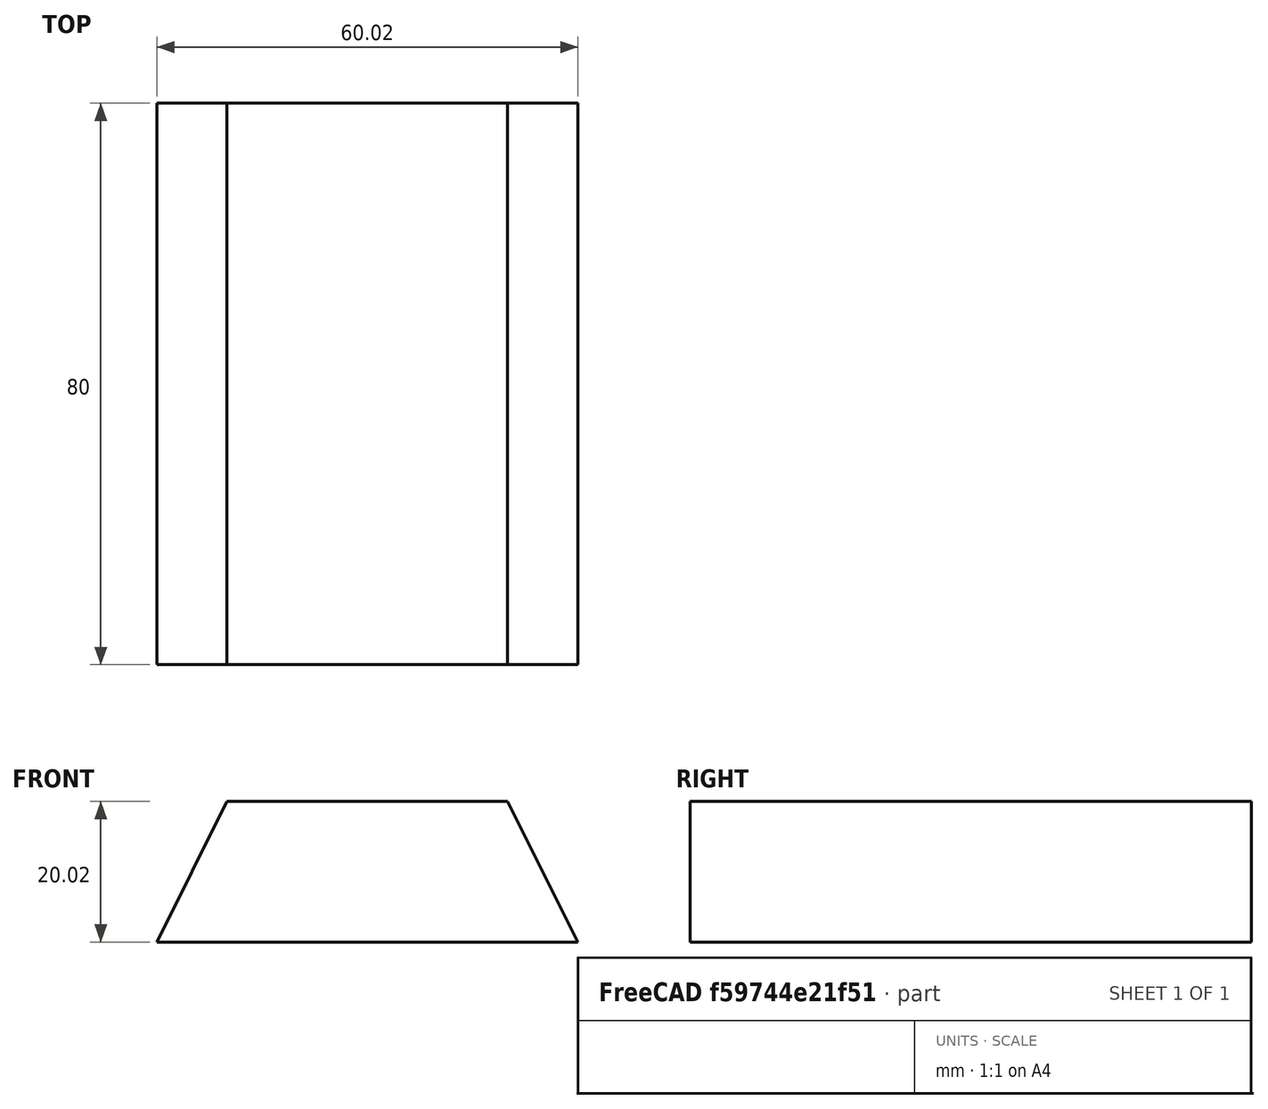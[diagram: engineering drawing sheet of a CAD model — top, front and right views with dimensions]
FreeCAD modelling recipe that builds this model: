
FCSTD DOCUMENT  (FreeCAD 0.21R33694 (Git))
Label: OJT1_T016R01_lingot_or
License: All rights reserved
LicenseURL: http://en.wikipedia.org/wiki/All_rights_reserved
objects: Sketcher::SketchObject×1, PartDesign::Pad×1, PartDesign::Body×1
note: 4 computed .brp shape members not serialized (recipe doc carries the construction recipe); baked Part::Feature solids carry a one-line shape summary decoded from their .brp

FEATURE [Sketcher::SketchObject] Sketch
  FullyConstrained = false
  MapMode = 5
  Support = -> [XY_Plane]
  sketch-geometry (4):
    g0: LineSegment StartX=-19.8368 StartY=20.0225 StartZ=0 EndX=20.1736 EndY=20.0225 EndZ=0
    g1: LineSegment StartX=20.1736 StartY=20.0225 StartZ=0 EndX=30.1762 EndY=0 EndZ=0
    g2: LineSegment StartX=30.1762 StartY=0 StartZ=0 EndX=-29.8394 EndY=0 EndZ=0
    g3: LineSegment StartX=-29.8394 StartY=0 StartZ=0 EndX=-19.8368 EndY=20.0225 EndZ=0
  constraints (8):
    c: Horizontal(g0)
    c: Coincident(g1,g0)
    c: PointOnObject(g1,g-1)
    c: Coincident(g2,g1)
    c: PointOnObject(g2,g-1)
    c: Horizontal(g2)
    c: Coincident(g3,g2)
    c: Coincident(g3,g0)
FEATURE [PartDesign::Pad] Pad
  Direction = (0,0,1)
  Length = 80
  Length2 = 10
  Profile = -> Sketch
  ReferenceAxis = -> Sketch [N_Axis]
  Type = 0
FEATURE [PartDesign::Body] Body
  Group = -> [Sketch,Pad]
  Origin = -> Origin
  Placement = pos=(0,0,0) rot=(1,0,0;1.5708rad)
  Tip = -> Pad
